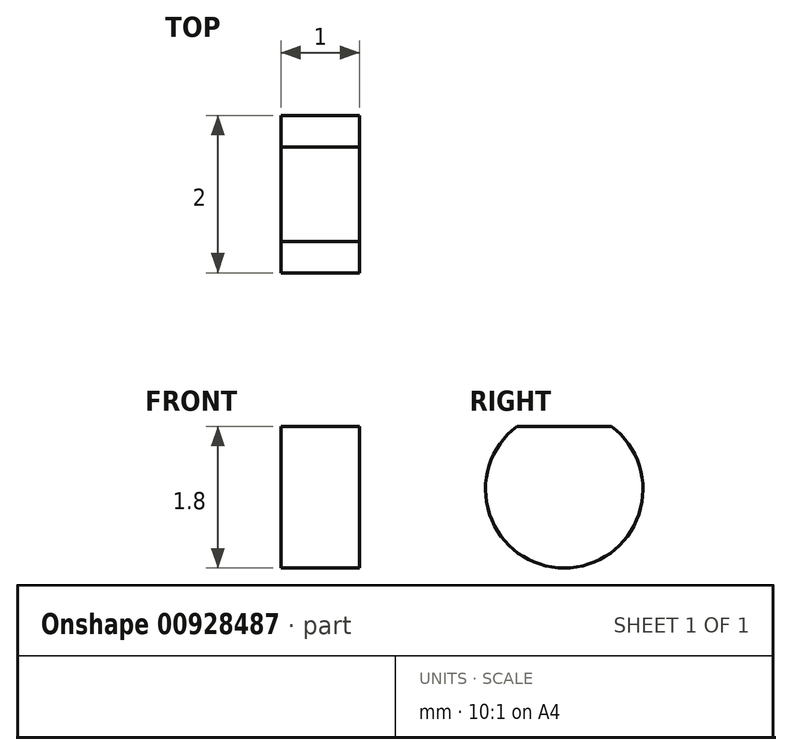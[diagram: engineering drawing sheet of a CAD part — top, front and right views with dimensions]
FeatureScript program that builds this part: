
annotation { "Feature Type Name" : "Feature", "Feature Type Description" : "" }
export const myFeature = defineFeature(function(context is Context, id is Id, definition is map)
    precondition{}
    {
        {
            var Q0;
            Q0=qCreatedBy(makeId("Right.planeOp"),FACE);
            var sketch = newSketch(context, id + "F0", { "sketchPlane" : qUnion([Q0])});
            skArc(sketch, "E0", {"start": v(-0.6, 0.8) * mm, "mid": v(0, -1) * mm, "end": v(0.6, 0.8) * mm});
            skLineSegment(sketch, "E1", {"start": v(-0.6, 0.8) * mm, "end": v(0.6, 0.8) * mm});
            skSolve(sketch);
        }
        {
            var Q0;
            Q0 = qSketchRegion(id + "F0", true);
            extrude(context, id + "F1", {"entities" : qUnion([Q0]), "depth" : 1 * mm, "offsetDistance" : 25 * mm});
        }
    });
